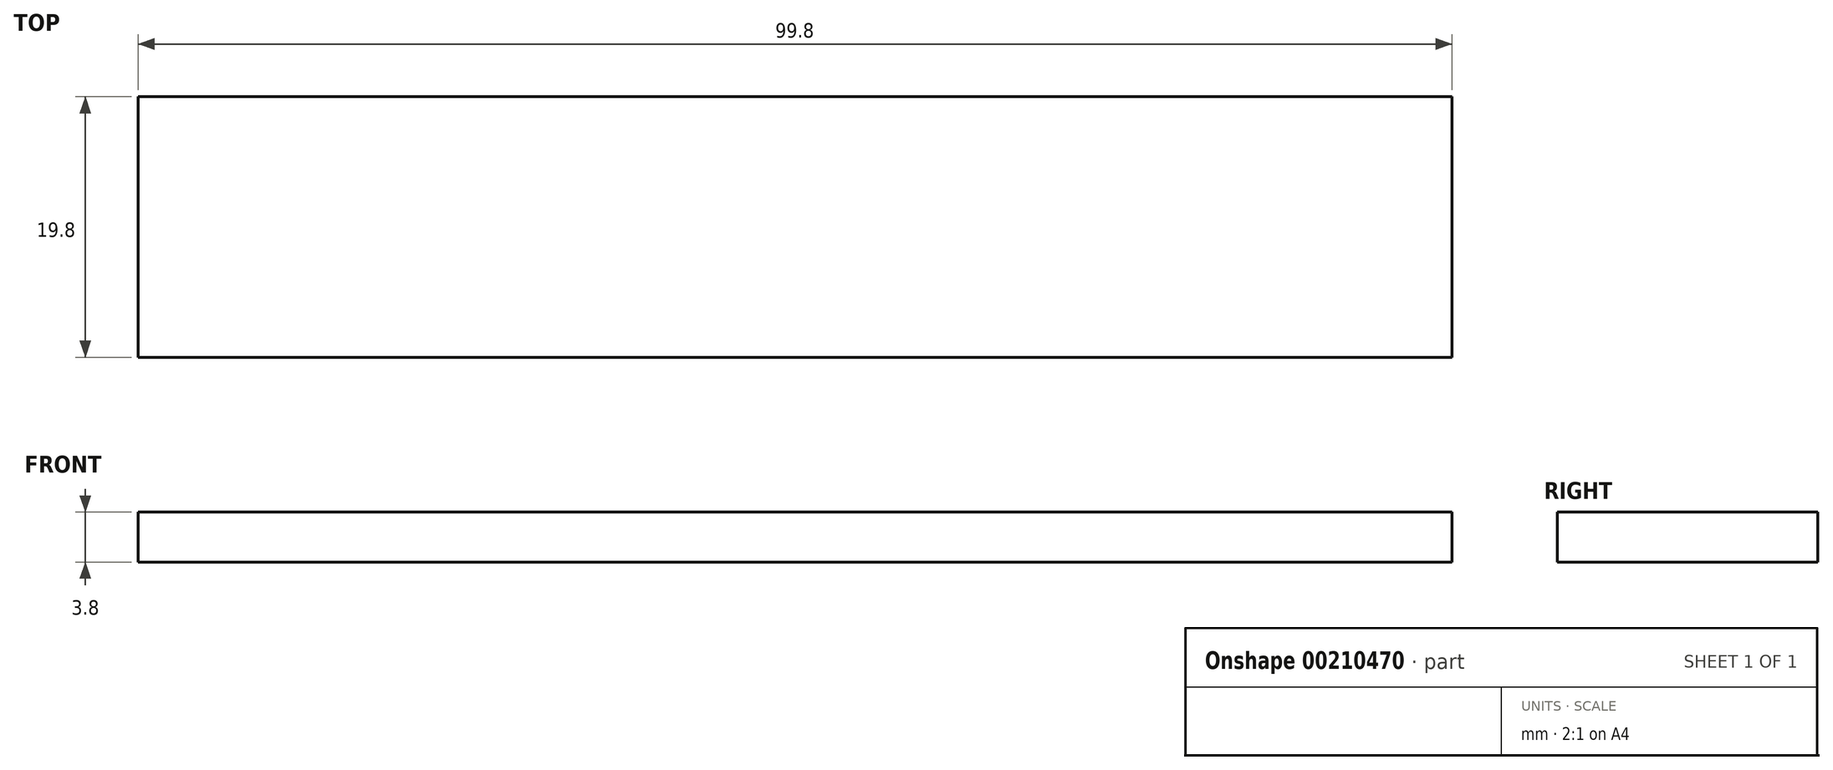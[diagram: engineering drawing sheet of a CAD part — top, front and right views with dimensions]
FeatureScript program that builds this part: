
annotation { "Feature Type Name" : "Feature", "Feature Type Description" : "" }
export const myFeature = defineFeature(function(context is Context, id is Id, definition is map)
    precondition{}
    {
        {
            var Q0;
            Q0=qCreatedBy(makeId("Top.planeOp"),FACE);
            var sketch = newSketch(context, id + "F0", { "sketchPlane" : qUnion([Q0])});
            skLineSegment(sketch, "E0.bottom", {"start": v(0, 0) * mm, "end": v(-99.8, 0) * mm});
            skLineSegment(sketch, "E0.top", {"start": v(0, 19.8) * mm, "end": v(-99.8, 19.8) * mm});
            skLineSegment(sketch, "E0.left", {"start": v(0, 0) * mm, "end": v(0, 19.8) * mm});
            skLineSegment(sketch, "E0.right", {"start": v(-99.8, 0) * mm, "end": v(-99.8, 19.8) * mm});
            skSolve(sketch);
        }
        {
            var Q0;
            Q0=makeQuery(id+"F0.imprint","IMPRINT",FACE,{"disambiguationData":[TD([[makeQuery(id+"F0.imprint","IMPRINT",EDGE,{"derivedFrom":sQuery(id+"F0.wireOp",EDGE,"E0.bottom")}),-1.0]])]});
            extrude(context, id + "F1", {"entities" : qUnion([Q0]), "depth" : 3.8 * mm});
        }
    });
